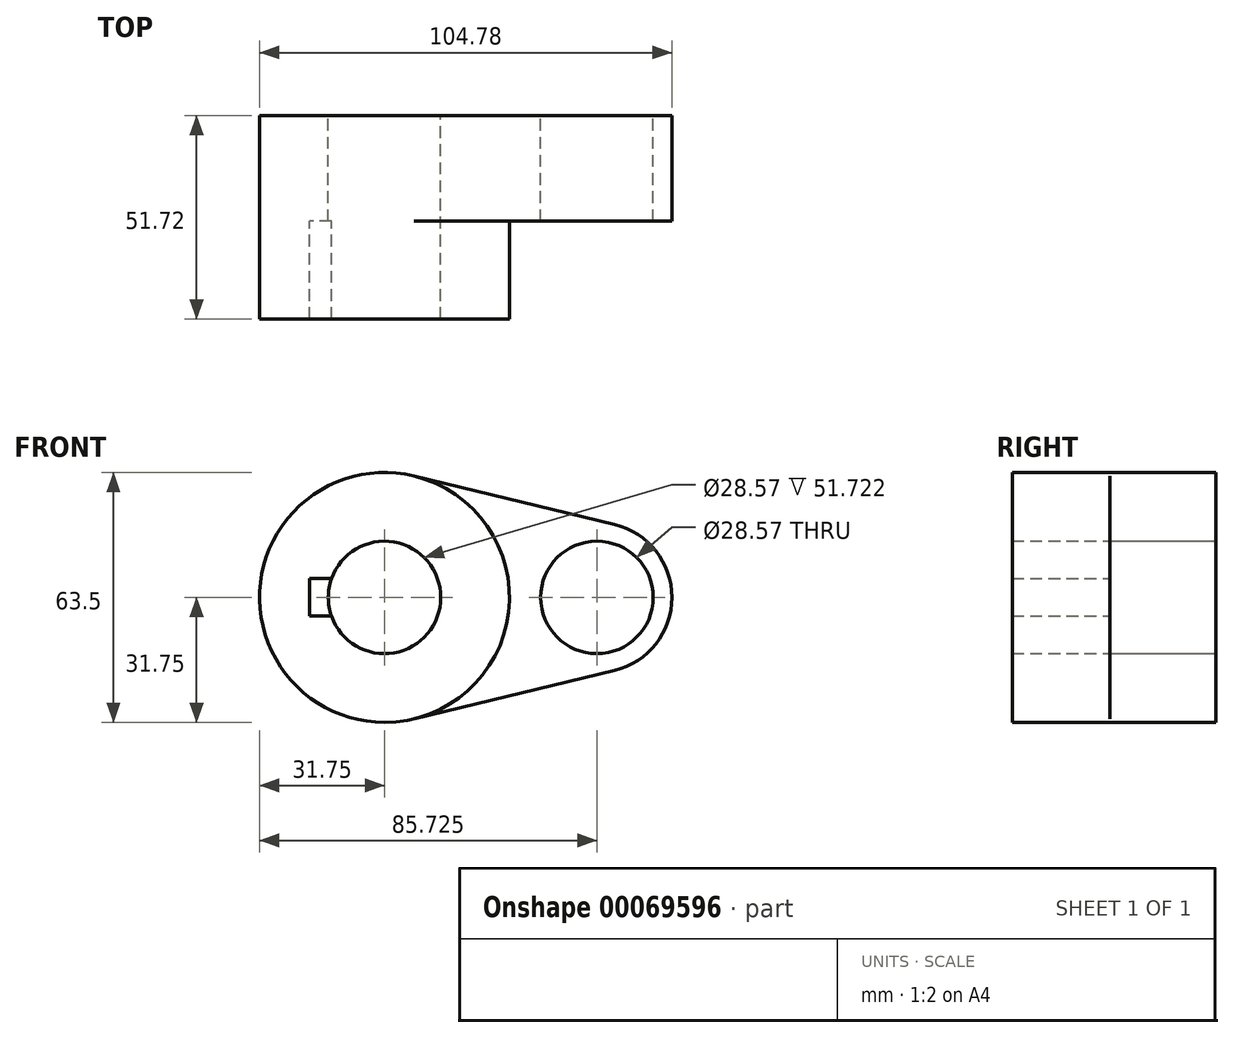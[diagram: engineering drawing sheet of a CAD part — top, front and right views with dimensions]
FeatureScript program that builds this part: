
annotation { "Feature Type Name" : "Feature", "Feature Type Description" : "" }
export const myFeature = defineFeature(function(context is Context, id is Id, definition is map)
    precondition{}
    {
        {
            var Q0;
            Q0=qCreatedBy(makeId("Front.planeOp"),FACE);
            var sketch = newSketch(context, id + "F0", { "sketchPlane" : qUnion([Q0])});
            skCircle(sketch, "E0", {"center": v(0, 0) * mm, "radius": 31.75 * mm});
            skCircle(sketch, "E1", {"center": v(53.98, 0) * mm, "radius": 19.05 * mm});
            skLineSegment(sketch, "E2", {"start": v(7.47, 30.86) * mm, "end": v(58.46, 18.52) * mm});
            skLineSegment(sketch, "E3", {"start": v(7.47, -30.86) * mm, "end": v(58.46, -18.52) * mm});
            skCircle(sketch, "E4", {"center": v(0, 0) * mm, "radius": 14.29 * mm});
            skCircle(sketch, "E5", {"center": v(53.98, 0) * mm, "radius": 14.29 * mm});
            skLineSegment(sketch, "E6.rect.bottom", {"start": v(-19.05, 4.76) * mm, "end": v(19.05, 4.76) * mm});
            skLineSegment(sketch, "E6.rect.top", {"start": v(-19.05, -4.76) * mm, "end": v(19.05, -4.76) * mm});
            skLineSegment(sketch, "E6.rect.left", {"start": v(-19.05, 4.76) * mm, "end": v(-19.05, -4.76) * mm});
            skLineSegment(sketch, "E6.rect.right", {"start": v(19.05, 4.76) * mm, "end": v(19.05, -4.76) * mm});
            skSolve(sketch);
        }
        {
            var Q0;
            {var subQ11=sQuery(id+"F0.wireOp",EDGE,"E6.rect.left");Q0=makeQuery(id+"F0.imprint","IMPRINT",FACE,{"disambiguationData":[TD([[makeQuery(id+"F0.imprint","IMPRINT",EDGE,{"derivedFrom":subQ11}),-1.0]])]});}
            var Q1;
            {var subQ5=sQuery(id+"F0.wireOp",EDGE,"E6.rect.right");Q1=makeQuery(id+"F0.imprint","IMPRINT",FACE,{"disambiguationData":[TD([[makeQuery(id+"F0.imprint","IMPRINT",EDGE,{"derivedFrom":subQ5}),-1.0]])]});}
            var Q2;
            Q2=makeQuery(id+"F0.imprint","IMPRINT",FACE,{"disambiguationData":[TD([[makeQuery(id+"F0.imprint","IMPRINT",EDGE,{"derivedFrom":sQuery(id+"F0.wireOp",EDGE,"E5")}),-1.0]])]});
            var Q3;
            {var subQ0=sQuery(id+"F0.wireOp",EDGE,"E2");Q3=makeQuery(id+"F0.imprint","IMPRINT",FACE,{"disambiguationData":[TD([[makeQuery(id+"F0.imprint","IMPRINT",EDGE,{"derivedFrom":subQ0}),-1.0]])]});}
            var Q4;
            {var subQ5=sQuery(id+"F0.wireOp",EDGE,"E6.rect.left");Q4=makeQuery(id+"F0.imprint","IMPRINT",FACE,{"disambiguationData":[TD([[makeQuery(id+"F0.imprint","IMPRINT",EDGE,{"derivedFrom":subQ5}),1.0]])]});}
            extrude(context, id + "F1", {"entities" : qUnion([Q0, Q1, Q2, Q3, Q4]), "depth" : 26.87 * mm});
        }
        {
            var Q0;
            {var subQ11=sQuery(id+"F0.wireOp",EDGE,"E6.rect.left");Q0=makeQuery(id+"F0.imprint","IMPRINT",FACE,{"disambiguationData":[TD([[makeQuery(id+"F0.imprint","IMPRINT",EDGE,{"derivedFrom":subQ11}),-1.0]])]});}
            var Q1;
            {var subQ5=sQuery(id+"F0.wireOp",EDGE,"E6.rect.right");Q1=makeQuery(id+"F0.imprint","IMPRINT",FACE,{"disambiguationData":[TD([[makeQuery(id+"F0.imprint","IMPRINT",EDGE,{"derivedFrom":subQ5}),-1.0]])]});}
            extrude(context, id + "F2", {"entities" : qUnion([Q0, Q1]), "operationType" : NewBodyOperationType.ADD, "depth" : 51.72 * mm});
        }
    });
